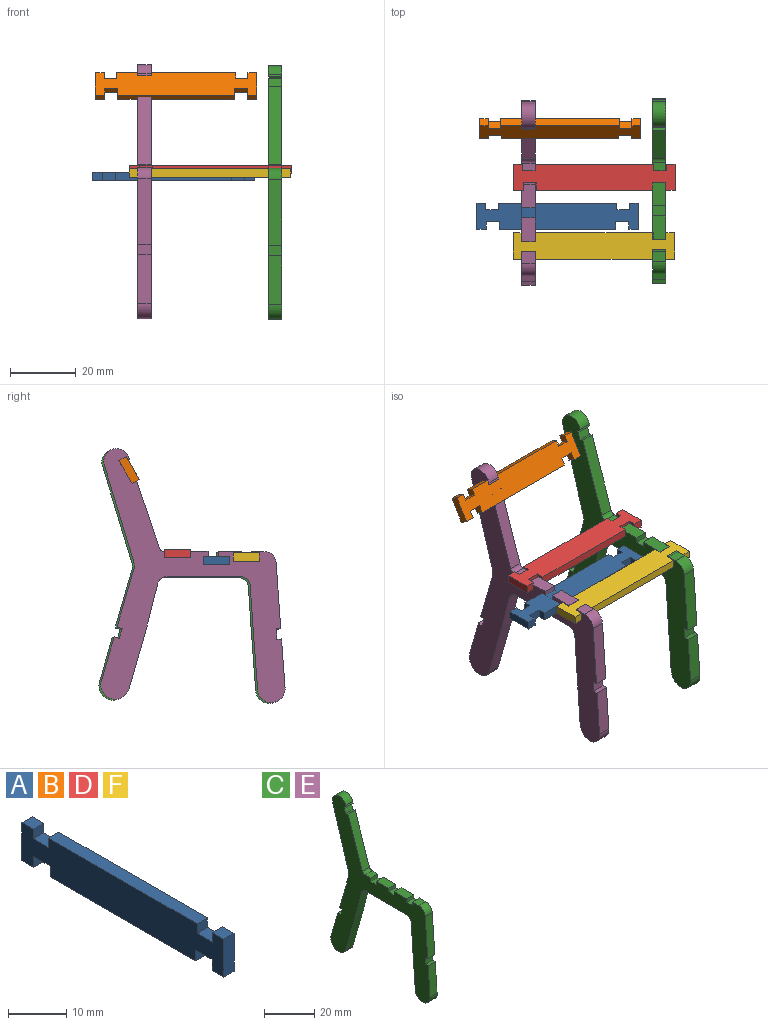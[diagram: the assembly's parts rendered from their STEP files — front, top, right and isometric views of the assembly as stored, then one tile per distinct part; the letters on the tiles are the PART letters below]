
ASSEMBLY  parts=6 mates=1
PART A: 22 faces, bbox 2.5x49.1x8 mm
  f0: plane 36.1x2.5mm, normal (0,0,1), area 90.2mm2, adj f1,f19,f20,f21
  f1: plane 2.5x2mm, normal (0,-1,0), area 5mm2, adj f0,f2,f20,f21
  f2: plane 3.75x2.5mm, normal (0,0,1), area 9.4mm2, adj f1,f3,f20,f21
  f3: plane 2.5x2mm, normal (0,1,0), area 5mm2, adj f2,f4,f20,f21
  f4: plane 2.73x2.5mm, normal (0,0,1), area 6.8mm2, adj f3,f5,f20,f21
  f5: plane 8x2.5mm, normal (0,-1,0), area 20mm2, adj f4,f6,f20,f21
  f6: plane 2.84x2.5mm, normal (0,0,-1), area 7.1mm2, adj f5,f7,f20,f21
  f7: plane 2.5x2.31mm, normal (0,1,0), area 5.8mm2, adj f6,f8,f20,f21
  f8: plane 4x2.5mm, normal (0,0,-1), area 10mm2, adj f7,f9,f20,f21
  f9: plane 2.5x2.3mm, normal (0,-1,0.01), area 5.7mm2, adj f8,f10,f20,f21
  f10: plane 35.41x2.5mm, normal (0,0,-1), area 88.5mm2, adj f9,f11,f20,f21
  f11: plane 2.5x2.3mm, normal (0,1,0.01), area 5.7mm2, adj f10,f12,f20,f21
  f12: plane 4x2.5mm, normal (0,0,-1), area 10mm2, adj f11,f13,f20,f21
  f13: plane 2.5x2.31mm, normal (0,-1,0), area 5.8mm2, adj f12,f14,f20,f21
  f14: plane 2.84x2.5mm, normal (0,0,-1), area 7.1mm2, adj f13,f15,f20,f21
  f15: plane 8x2.5mm, normal (0,1,0), area 20mm2, adj f14,f16,f20,f21
  f16: plane 2.73x2.5mm, normal (0,0,1), area 6.8mm2, adj f15,f17,f20,f21
  f17: plane 2.5x2mm, normal (0,-1,0), area 5mm2, adj f16,f18,f20,f21
  f18: plane 3.75x2.5mm, normal (0,0,1), area 9.4mm2, adj f17,f19,f20,f21
  f19: plane 2.5x2mm, normal (0,1,0), area 5mm2, adj f0,f18,f20,f21
  f20: plane 49.06x8mm, normal (1,0,0), area 359.1mm2, adj f0,f1,f2,f3,f4,f5,f6,f7
  f21: plane 49.06x8mm, normal (-1,0,0), area 359.1mm2, adj f0,f1,f2,f3,f4,f5,f6,f7
PART B: same geometry as A
PART C: 44 faces, bbox 4x56x77.2 mm
  f0: plane 4x3mm, normal (0,0,1), area 12mm2, adj f1,f41,f42,f43
  f1: plane 4x1.66mm, normal (0,1,0), area 6.6mm2, adj f0,f2,f42,f43
  f2: plane 6.98x4mm, normal (0,0,1), area 27.9mm2, adj f1,f3,f42,f43
  f3: plane 4x1.6mm, normal (0,-1,0), area 6.4mm2, adj f2,f4,f42,f43
  f4: plane 4x3.08mm, normal (0,0,1), area 12.3mm2, adj f3,f5,f42,f43
  f5: plane 4x1.6mm, normal (0,1,0), area 6.4mm2, adj f4,f6,f42,f43
  f6: plane 7.19x4mm, normal (0,0,1), area 28.8mm2, adj f5,f7,f42,f43
  f7: plane 4x1.66mm, normal (0,-1,0), area 6.6mm2, adj f6,f8,f42,f43
  f8: plane 4x3.08mm, normal (0,0,1), area 12.3mm2, adj f7,f9,f42,f43
  f9: plane 4x1.66mm, normal (0,1,0), area 6.6mm2, adj f8,f10,f42,f43
  f10: plane 4x3.66mm, normal (0,0,1), area 14.6mm2, adj f9,f11,f42,f43
  f11: cylinder r=3.69mm len=4mm, axis (-1,0,0), area 22.1mm2, adj f10,f12,f42,f43
  f12: plane 19.95x4mm, normal (0,-1,0.07), area 80mm2, adj f11,f13,f42,f43
  f13: plane 4x1.35mm, normal (0,-0.07,-1), area 5.4mm2, adj f12,f14,f42,f43
  f14: plane 4x3.22mm, normal (0,-1,0.05), area 12.9mm2, adj f13,f15,f42,f43
  f15: plane 4x1.43mm, normal (0,0.07,1), area 5.8mm2, adj f14,f16,f42,f43
  f16: plane 14.87x4mm, normal (0,-1,0.07), area 59.6mm2, adj f15,f17,f42,f43
  f17: cylinder r=4.18mm len=8.34mm, axis (-1,0,0), area 52.5mm2, adj f16,f18,f42,f43
  f18: plane 19.01x4mm, normal (0,1,-0.07), area 76.3mm2, adj f17,f19,f42,f43
  f19: plane 12.59x4mm, normal (0,1,-0.07), area 50.5mm2, adj f18,f20,f42,f43
  f20: cylinder r=3mm len=4mm, axis (-1,0,0), area 18mm2, adj f19,f21,f42,f43
  f21: plane 22.27x4mm, normal (0,0,-1), area 89.1mm2, adj f20,f22,f42,f43
  f22: cylinder r=3mm len=4mm, axis (-1,0,0), area 15.9mm2, adj f21,f23,f42,f43
  f23: plane 13.36x4mm, normal (0,-0.97,-0.24), area 55.1mm2, adj f22,f24,f42,f43
  f24: plane 18.37x5.28mm, normal (0,-0.96,-0.28), area 76.5mm2, adj f23,f25,f42,f43
  f25: cylinder r=4.36mm len=8.59mm, axis (-1,0,0), area 54.8mm2, adj f24,f26,f42,f43
  f26: plane 13.51x4mm, normal (0,0.96,0.28), area 56.2mm2, adj f25,f27,f42,f43
  f27: plane 4x1.52mm, normal (0,-0.28,0.96), area 6.3mm2, adj f26,f28,f42,f43
  f28: plane 4x2.96mm, normal (0,0.96,0.28), area 12.3mm2, adj f27,f29,f42,f43
  f29: plane 4x1.52mm, normal (0,0.28,-0.96), area 6.3mm2, adj f28,f30,f42,f43
  f30: plane 17.87x5.17mm, normal (0,0.96,0.28), area 74.4mm2, adj f29,f31,f42,f43
  f31: cylinder r=3mm len=4mm, axis (-1,0,0), area 6.9mm2, adj f30,f32,f42,f43
  f32: plane 29.45x8.92mm, normal (0,0.96,-0.29), area 123.1mm2, adj f31,f33,f42,f43
  f33: cylinder r=3.86mm len=7.58mm, axis (-1,0,0), area 50.2mm2, adj f32,f34,f42,f43
  f34: plane 4x0.63mm, normal (0,-0.95,0.32), area 2.7mm2, adj f33,f35,f42,f43
  f35: plane 4x1.23mm, normal (0,-0.32,-0.95), area 5.2mm2, adj f34,f36,f42,f43
  f36: plane 4x2.88mm, normal (0,-0.95,0.32), area 12.2mm2, adj f35,f37,f42,f43
  f37: plane 4x1.23mm, normal (0,0.32,0.95), area 5.2mm2, adj f36,f38,f42,f43
  f38: plane 23.92x8.16mm, normal (0,-0.95,0.32), area 101.1mm2, adj f37,f39,f42,f43
  f39: cylinder r=1.52mm len=4mm, axis (-1,0,0), area 7.5mm2, adj f38,f40,f42,f43
  f40: plane 4x3.34mm, normal (0,0,1), area 13.4mm2, adj f39,f41,f42,f43
  f41: plane 4x1.66mm, normal (0,-1,0), area 6.6mm2, adj f0,f40,f42,f43
  f42: plane 77.22x55.99mm, normal (1,0,0), area 1201.9mm2, adj f0,f1,f2,f3,f4,f5,f6,f7
  f43: plane 77.22x55.99mm, normal (-1,0,0), area 1201.9mm2, adj f0,f1,f2,f3,f4,f5,f6,f7
PART D: same geometry as A
PART E: same geometry as C
PART F: same geometry as A
PLACE A rot(axis=(-0.58,-0.58,-0.58),120deg) t=(6.1,-62.92,18.94)mm
PLACE B rot(axis=(-0.25,-0.25,-0.94),93.8deg) t=(6.9,-18.57,18.02)mm
PLACE C at identity fixed
PLACE D rot(axis=(-0.58,-0.58,-0.58),120deg) t=(17.3,-51.12,20.92)mm
PLACE E t=(-39.73,-0.58,0.26)mm
PLACE F rot(axis=(-0.58,-0.58,-0.58),120deg) t=(17.15,-71.97,19.91)mm
MATE planar D.f21 <-> C.f0  axis (0,0,-1) through (4,-19.36,20.92)mm
